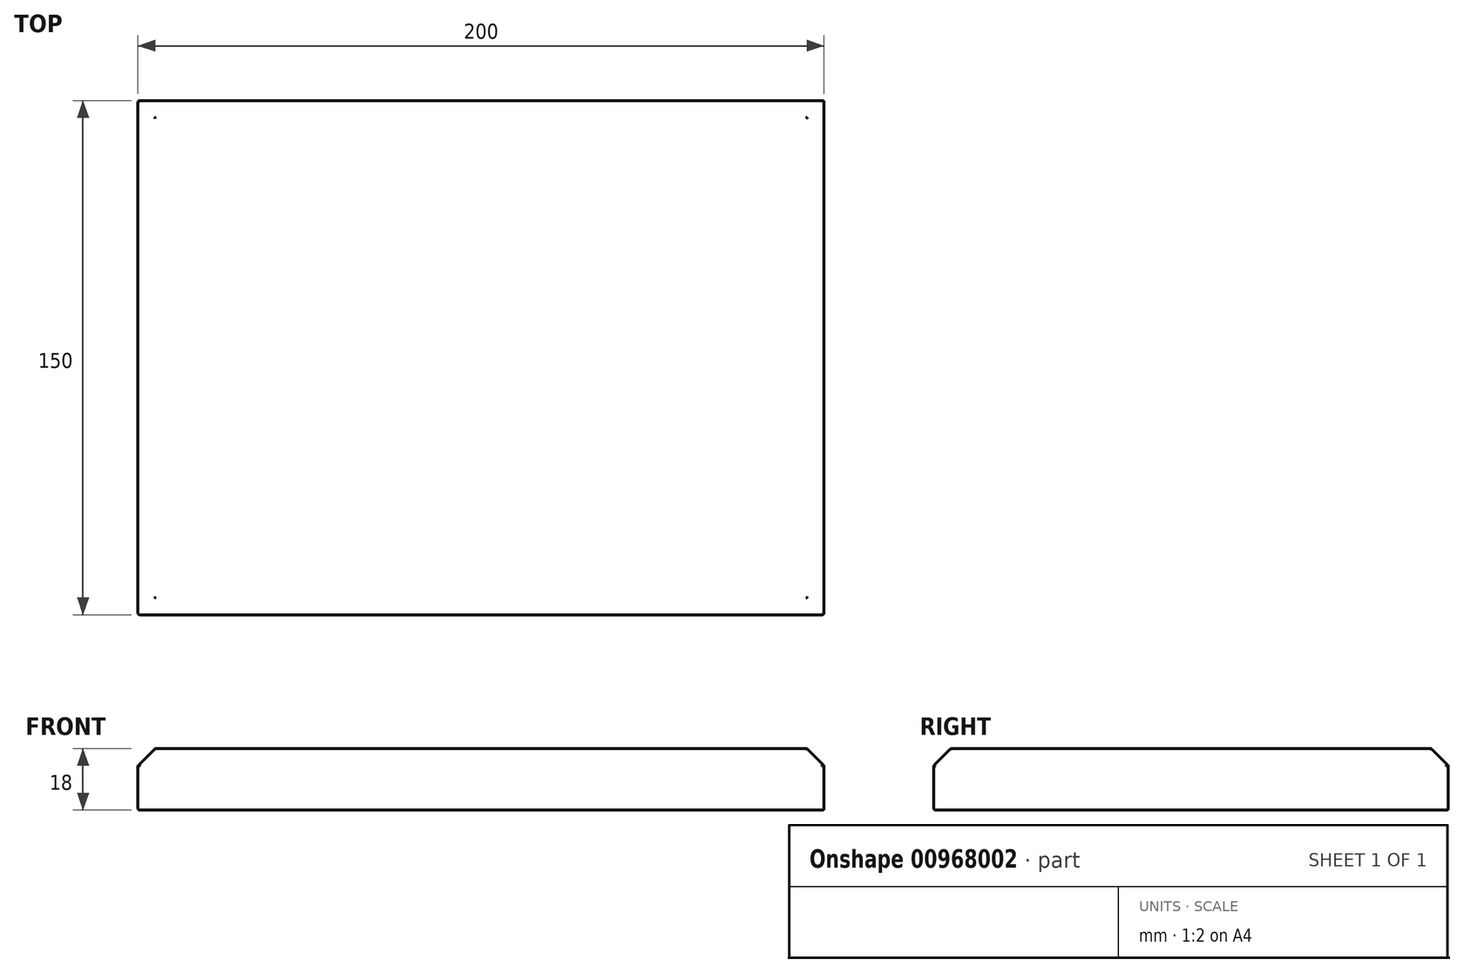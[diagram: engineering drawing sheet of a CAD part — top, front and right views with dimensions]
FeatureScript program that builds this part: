
annotation { "Feature Type Name" : "Feature", "Feature Type Description" : "" }
export const myFeature = defineFeature(function(context is Context, id is Id, definition is map)
    precondition{}
    {
        {
            var Q0;
            Q0=qCreatedBy(makeId("Top.planeOp"),FACE);
            var sketch = newSketch(context, id + "F0", { "sketchPlane" : qUnion([Q0])});
            skLineSegment(sketch, "E0", {"start": v(-100, 0) * mm, "end": v(-100, 75) * mm});
            skLineSegment(sketch, "E1", {"start": v(-100, 75) * mm, "end": v(100, 75) * mm});
            skLineSegment(sketch, "E2", {"start": v(100, 75) * mm, "end": v(100, -75) * mm});
            skLineSegment(sketch, "E3", {"start": v(100, -75) * mm, "end": v(-100, -75) * mm});
            skLineSegment(sketch, "E4", {"start": v(-100, -75) * mm, "end": v(-100, 0) * mm});
            skSolve(sketch);
        }
        {
            var Q0;
            Q0=makeQuery(id+"F0.imprint","IMPRINT",FACE,{"disambiguationData":[TD([[makeQuery(id+"F0.imprint","IMPRINT",EDGE,{"derivedFrom":sQuery(id+"F0.wireOp",EDGE,"E0")}),-1.0]])]});
            extrude(context, id + "F1", {"entities" : qUnion([Q0]), "depth" : 18 * mm, "offsetDistance" : 25 * mm});
        }
        {
            var Q0;
            Q0=makeQuery(id+"F1.opExtrude","CAP_EDGE",EDGE,{"disambiguationData":[OSD([sQuery(id+"F0.wireOp",EDGE,"E3")])],"isStart":false});
            var Q1;
            Q1=makeQuery(id+"F1.opExtrude","CAP_EDGE",EDGE,{"disambiguationData":[OSD([sQuery(id+"F0.wireOp",EDGE,"E0"),sQuery(id+"F0.wireOp",EDGE,"E4")])],"isStart":false});
            var Q2;
            Q2=makeQuery(id+"F1.opExtrude","CAP_EDGE",EDGE,{"disambiguationData":[OSD([sQuery(id+"F0.wireOp",EDGE,"E2")])],"isStart":false});
            var Q3;
            Q3=makeQuery(id+"F1.opExtrude","CAP_FACE",FACE,{"disambiguationData":[OSD([sQuery(id+"F0.wireOp",EDGE,"E0"),sQuery(id+"F0.wireOp",EDGE,"E1"),sQuery(id+"F0.wireOp",EDGE,"E2"),sQuery(id+"F0.wireOp",EDGE,"E3"),sQuery(id+"F0.wireOp",EDGE,"E4")])],"isStart":false});
            chamfer(context, id + "F2", {"entities" : qUnion([Q0, Q1, Q2, Q3]), "width" : 5 * mm, "tangentPropagation" : true});
        }
        {
            var Q0;
            {var subQ0=sQuery(id+"F0.wireOp",EDGE,"E3");Q0=makeQuery(id+"F2.opChamfer","BLEND_EDGE",EDGE,{"blendedFrom":[makeQuery(id+"F1.opExtrude","CAP_EDGE",EDGE,{"disambiguationData":[OSD([subQ0])],"isStart":false}),makeQuery(id+"F1.opExtrude","CAP_FACE",FACE,{"disambiguationData":[OSD([sQuery(id+"F0.wireOp",EDGE,"E0"),sQuery(id+"F0.wireOp",EDGE,"E1"),sQuery(id+"F0.wireOp",EDGE,"E2"),subQ0,sQuery(id+"F0.wireOp",EDGE,"E4")])],"isStart":false})],"blendedInto":[makeQuery(id+"F1.opExtrude","CAP_FACE",FACE,{"disambiguationData":[OSD([sQuery(id+"F0.wireOp",EDGE,"E0"),sQuery(id+"F0.wireOp",EDGE,"E1"),sQuery(id+"F0.wireOp",EDGE,"E2"),subQ0,sQuery(id+"F0.wireOp",EDGE,"E4")])],"isStart":false})]});}
            var Q1;
            {var subQ0=sQuery(id+"F0.wireOp",EDGE,"E2");Q1=makeQuery(id+"F2.opChamfer","BLEND_EDGE",EDGE,{"blendedFrom":[makeQuery(id+"F1.opExtrude","CAP_EDGE",EDGE,{"disambiguationData":[OSD([subQ0])],"isStart":false}),makeQuery(id+"F1.opExtrude","CAP_FACE",FACE,{"disambiguationData":[OSD([sQuery(id+"F0.wireOp",EDGE,"E0"),sQuery(id+"F0.wireOp",EDGE,"E1"),subQ0,sQuery(id+"F0.wireOp",EDGE,"E3"),sQuery(id+"F0.wireOp",EDGE,"E4")])],"isStart":false})],"blendedInto":[makeQuery(id+"F1.opExtrude","CAP_FACE",FACE,{"disambiguationData":[OSD([sQuery(id+"F0.wireOp",EDGE,"E0"),sQuery(id+"F0.wireOp",EDGE,"E1"),subQ0,sQuery(id+"F0.wireOp",EDGE,"E3"),sQuery(id+"F0.wireOp",EDGE,"E4")])],"isStart":false})]});}
            var Q2;
            {var subQ0=sQuery(id+"F0.wireOp",EDGE,"E2");Q2=makeQuery(id+"F2.opChamfer","BLEND_EDGE",EDGE,{"blendedFrom":[makeQuery(id+"F1.opExtrude","CAP_EDGE",EDGE,{"disambiguationData":[OSD([subQ0])],"isStart":false}),makeQuery(id+"F1.opExtrude","SWEPT_FACE",FACE,{"disambiguationData":[OSD([subQ0])]})],"blendedInto":[makeQuery(id+"F1.opExtrude","SWEPT_FACE",FACE,{"disambiguationData":[OSD([subQ0])]})]});}
            var Q3;
            {var subQ0=sQuery(id+"F0.wireOp",EDGE,"E1");Q3=makeQuery(id+"F2.opChamfer","BLEND_EDGE",EDGE,{"blendedFrom":[makeQuery(id+"F1.opExtrude","CAP_EDGE",EDGE,{"disambiguationData":[OSD([subQ0])],"isStart":false}),makeQuery(id+"F1.opExtrude","CAP_FACE",FACE,{"disambiguationData":[OSD([sQuery(id+"F0.wireOp",EDGE,"E0"),subQ0,sQuery(id+"F0.wireOp",EDGE,"E2"),sQuery(id+"F0.wireOp",EDGE,"E3"),sQuery(id+"F0.wireOp",EDGE,"E4")])],"isStart":false})],"blendedInto":[makeQuery(id+"F1.opExtrude","CAP_FACE",FACE,{"disambiguationData":[OSD([sQuery(id+"F0.wireOp",EDGE,"E0"),subQ0,sQuery(id+"F0.wireOp",EDGE,"E2"),sQuery(id+"F0.wireOp",EDGE,"E3"),sQuery(id+"F0.wireOp",EDGE,"E4")])],"isStart":false})]});}
            var Q4;
            {var subQ0=sQuery(id+"F0.wireOp",EDGE,"E1");Q4=makeQuery(id+"F2.opChamfer","BLEND_EDGE",EDGE,{"blendedFrom":[makeQuery(id+"F1.opExtrude","CAP_EDGE",EDGE,{"disambiguationData":[OSD([subQ0])],"isStart":false}),makeQuery(id+"F1.opExtrude","SWEPT_FACE",FACE,{"disambiguationData":[OSD([subQ0])]})],"blendedInto":[makeQuery(id+"F1.opExtrude","SWEPT_FACE",FACE,{"disambiguationData":[OSD([subQ0])]})]});}
            var Q5;
            Q5=makeQuery(id+"F2.opChamfer","BLEND_FACE",FACE,{"disambiguationData":[OSD([sQuery(id+"F0.wireOp",EDGE,"E0"),sQuery(id+"F0.wireOp",EDGE,"E4")])]});
            var Q6;
            {var subQ0=sQuery(id+"F0.wireOp",EDGE,"E4");var subQ1=sQuery(id+"F0.wireOp",EDGE,"E0");Q6=makeQuery(id+"F2.opChamfer","BLEND_EDGE",EDGE,{"blendedFrom":[makeQuery(id+"F1.opExtrude","CAP_EDGE",EDGE,{"disambiguationData":[OSD([subQ1,subQ0])],"isStart":false}),makeQuery(id+"F1.opExtrude","SWEPT_FACE",FACE,{"disambiguationData":[OSD([subQ1,subQ0])]})],"blendedInto":[makeQuery(id+"F1.opExtrude","SWEPT_FACE",FACE,{"disambiguationData":[OSD([subQ1,subQ0])]})]});}
            var Q7;
            Q7=makeQuery(id+"F2.opChamfer","BLEND_EDGE",EDGE,{"blendedFrom":[makeQuery(id+"F1.opExtrude","CAP_EDGE",EDGE,{"disambiguationData":[OSD([sQuery(id+"F0.wireOp",EDGE,"E0"),sQuery(id+"F0.wireOp",EDGE,"E4")])],"isStart":false}),makeQuery(id+"F1.opExtrude","CAP_EDGE",EDGE,{"disambiguationData":[OSD([sQuery(id+"F0.wireOp",EDGE,"E1")])],"isStart":false})],"blendedInto":[]});
            var Q8;
            Q8=makeQuery(id+"F2.opChamfer","BLEND_EDGE",EDGE,{"blendedFrom":[makeQuery(id+"F1.opExtrude","CAP_EDGE",EDGE,{"disambiguationData":[OSD([sQuery(id+"F0.wireOp",EDGE,"E0"),sQuery(id+"F0.wireOp",EDGE,"E4")])],"isStart":false}),makeQuery(id+"F1.opExtrude","CAP_EDGE",EDGE,{"disambiguationData":[OSD([sQuery(id+"F0.wireOp",EDGE,"E3")])],"isStart":false})],"blendedInto":[]});
            var Q9;
            Q9=makeQuery(id+"F2.opChamfer","BLEND_EDGE",EDGE,{"blendedFrom":[makeQuery(id+"F1.opExtrude","CAP_EDGE",EDGE,{"disambiguationData":[OSD([sQuery(id+"F0.wireOp",EDGE,"E2")])],"isStart":false}),makeQuery(id+"F1.opExtrude","CAP_EDGE",EDGE,{"disambiguationData":[OSD([sQuery(id+"F0.wireOp",EDGE,"E3")])],"isStart":false})],"blendedInto":[]});
            var Q10;
            Q10=makeQuery(id+"F1.opExtrude","SWEPT_EDGE",EDGE,{"disambiguationData":[OSD([sQuery(id+"F0.wireOp",EDGE,"E2"),sQuery(id+"F0.wireOp",EDGE,"E3")])]});
            var Q11;
            Q11=makeQuery(id+"F2.opChamfer","BLEND_EDGE",EDGE,{"blendedFrom":[makeQuery(id+"F1.opExtrude","CAP_EDGE",EDGE,{"disambiguationData":[OSD([sQuery(id+"F0.wireOp",EDGE,"E1")])],"isStart":false}),makeQuery(id+"F1.opExtrude","CAP_EDGE",EDGE,{"disambiguationData":[OSD([sQuery(id+"F0.wireOp",EDGE,"E2")])],"isStart":false})],"blendedInto":[]});
            var Q12;
            Q12=makeQuery(id+"F1.opExtrude","SWEPT_EDGE",EDGE,{"disambiguationData":[OSD([sQuery(id+"F0.wireOp",EDGE,"E1"),sQuery(id+"F0.wireOp",EDGE,"E2")])]});
            var Q13;
            Q13=makeQuery(id+"F1.opExtrude","SWEPT_EDGE",EDGE,{"disambiguationData":[OSD([sQuery(id+"F0.wireOp",EDGE,"E0"),sQuery(id+"F0.wireOp",EDGE,"E1")])]});
            var Q14;
            Q14=makeQuery(id+"F1.opExtrude","SWEPT_EDGE",EDGE,{"disambiguationData":[OSD([sQuery(id+"F0.wireOp",EDGE,"E3"),sQuery(id+"F0.wireOp",EDGE,"E4")])]});
            var Q15;
            {var subQ0=sQuery(id+"F0.wireOp",EDGE,"E3");Q15=makeQuery(id+"F2.opChamfer","BLEND_EDGE",EDGE,{"blendedFrom":[makeQuery(id+"F1.opExtrude","CAP_EDGE",EDGE,{"disambiguationData":[OSD([subQ0])],"isStart":false}),makeQuery(id+"F1.opExtrude","SWEPT_FACE",FACE,{"disambiguationData":[OSD([subQ0])]})],"blendedInto":[makeQuery(id+"F1.opExtrude","SWEPT_FACE",FACE,{"disambiguationData":[OSD([subQ0])]})]});}
            var Q16;
            Q16=makeQuery(id+"F1.opExtrude","CAP_EDGE",EDGE,{"disambiguationData":[OSD([sQuery(id+"F0.wireOp",EDGE,"E3")])],"isStart":true});
            var Q17;
            Q17=makeQuery(id+"F1.opExtrude","CAP_EDGE",EDGE,{"disambiguationData":[OSD([sQuery(id+"F0.wireOp",EDGE,"E0"),sQuery(id+"F0.wireOp",EDGE,"E4")])],"isStart":true});
            var Q18;
            Q18=makeQuery(id+"F1.opExtrude","CAP_EDGE",EDGE,{"disambiguationData":[OSD([sQuery(id+"F0.wireOp",EDGE,"E1")])],"isStart":true});
            var Q19;
            Q19=makeQuery(id+"F1.opExtrude","CAP_EDGE",EDGE,{"disambiguationData":[OSD([sQuery(id+"F0.wireOp",EDGE,"E2")])],"isStart":true});
            fillet(context, id + "F3", {"entities" : qUnion([Q0, Q1, Q2, Q3, Q4, Q5, Q6, Q7, Q8, Q9, Q10, Q11, Q12, Q13, Q14, Q15, Q16, Q17, Q18, Q19]), "radius" : .5 * mm, "tangentPropagation" : true, "allowEdgeOverflow" : false});
        }
    });
